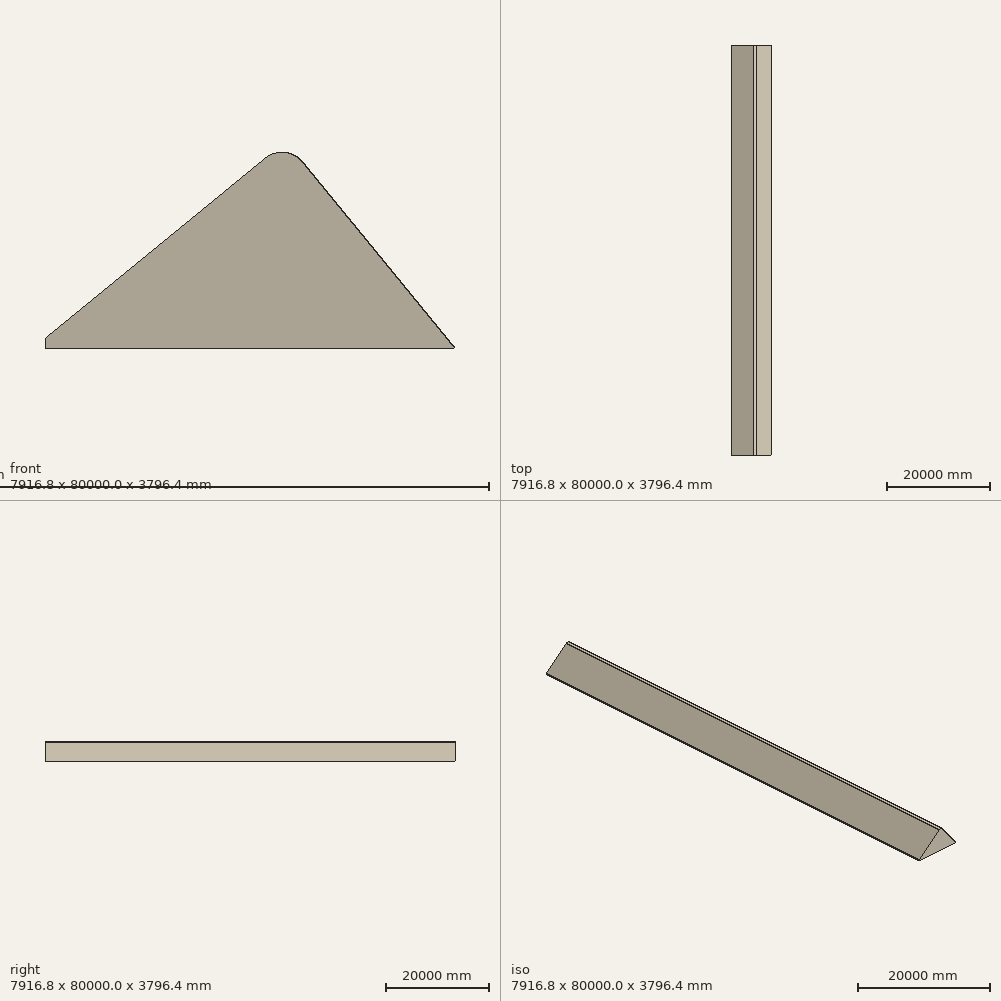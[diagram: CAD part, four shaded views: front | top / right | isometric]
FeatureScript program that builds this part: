
annotation { "Feature Type Name" : "Feature", "Feature Type Description" : "" }
export const myFeature = defineFeature(function(context is Context, id is Id, definition is map)
    precondition{}
    {
        {
            var Q0;
            Q0=qCreatedBy(makeId("Front.planeOp"),FACE);
            var sketch = newSketch(context, id + "F0", { "sketchPlane" : qUnion([Q0])});
            skLineSegment(sketch, "E0", {"start": v(0, 0) * mm, "end": v(0, 200) * mm});
            skLineSegment(sketch, "E1", {"start": v(0, 200) * mm, "end": v(4643.27, 4000) * mm});
            skLineSegment(sketch, "E2", {"start": v(4643.27, 4000) * mm, "end": v(7916.83, 0) * mm});
            skLineSegment(sketch, "E3", {"start": v(0, 0) * mm, "end": v(7916.83, 0) * mm});
            skSolve(sketch);
        }
        {
            var Q0;
            Q0=makeQuery(id+"F0.imprint","IMPRINT",FACE,{"disambiguationData":[TD([[makeQuery(id+"F0.imprint","IMPRINT",EDGE,{"derivedFrom":sQuery(id+"F0.wireOp",EDGE,"E0")}),-1.0]])]});
            extrude(context, id + "F1", {"entities" : qUnion([Q0]), "depth" : 80000 * mm, "offsetDistance" : 25 * mm});
        }
        {
            var Q0;
            Q0=makeQuery(id+"F1.opExtrude","SWEPT_EDGE",EDGE,{"disambiguationData":[OSD([sQuery(id+"F0.wireOp",EDGE,"E1"),sQuery(id+"F0.wireOp",EDGE,"E2")])]});
            fillet(context, id + "F2", {"entities" : qUnion([Q0]), "radius" : 500 * mm, "tangentPropagation" : true, "allowEdgeOverflow" : false});
        }
    });
